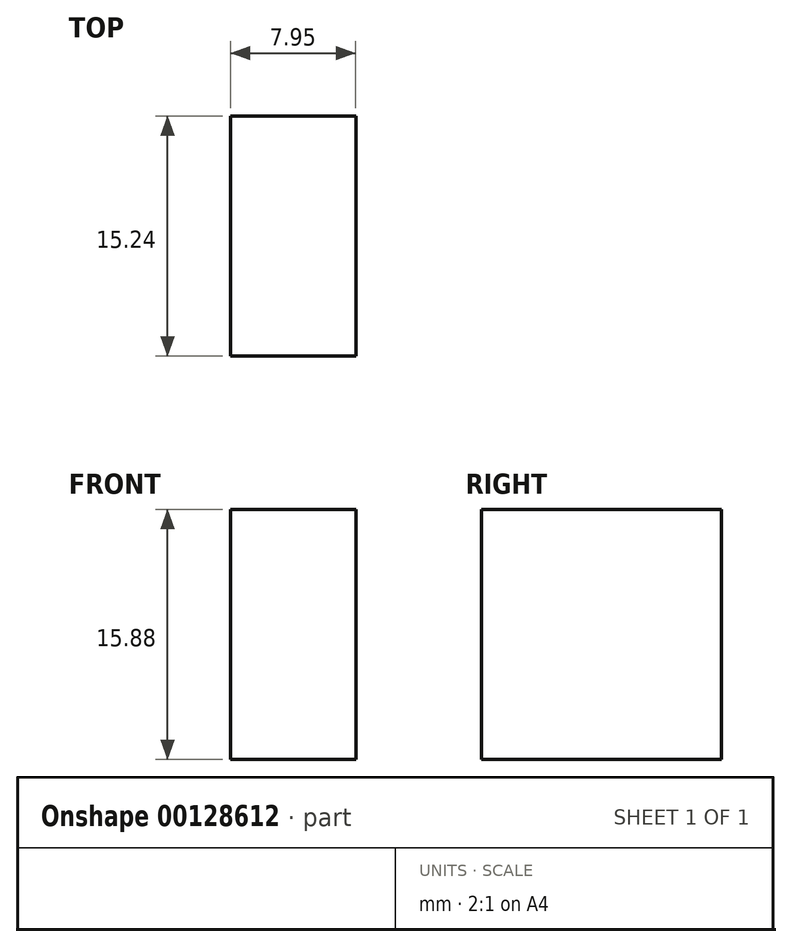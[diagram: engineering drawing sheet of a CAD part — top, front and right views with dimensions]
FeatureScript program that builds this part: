
annotation { "Feature Type Name" : "Feature", "Feature Type Description" : "" }
export const myFeature = defineFeature(function(context is Context, id is Id, definition is map)
    precondition{}
    {
        {
            var Q0;
            Q0=qCreatedBy(makeId("Front.planeOp"),FACE);
            var sketch = newSketch(context, id + "F0", { "sketchPlane" : qUnion([Q0])});
            skLineSegment(sketch, "E0.bottom", {"start": v(-32.29, 0) * mm, "end": v(-24.34, 0) * mm});
            skLineSegment(sketch, "E0.top", {"start": v(-32.29, 15.88) * mm, "end": v(-24.34, 15.88) * mm});
            skLineSegment(sketch, "E0.left", {"start": v(-32.29, 0) * mm, "end": v(-32.29, 15.88) * mm});
            skLineSegment(sketch, "E0.right", {"start": v(-24.34, 0) * mm, "end": v(-24.34, 15.88) * mm});
            skSolve(sketch);
        }
        {
            var Q0;
            Q0 = qSketchRegion(id + "F0", true);
            extrude(context, id + "F1", {"entities" : qUnion([Q0]), "depth" : 15.24 * mm});
        }
    });
